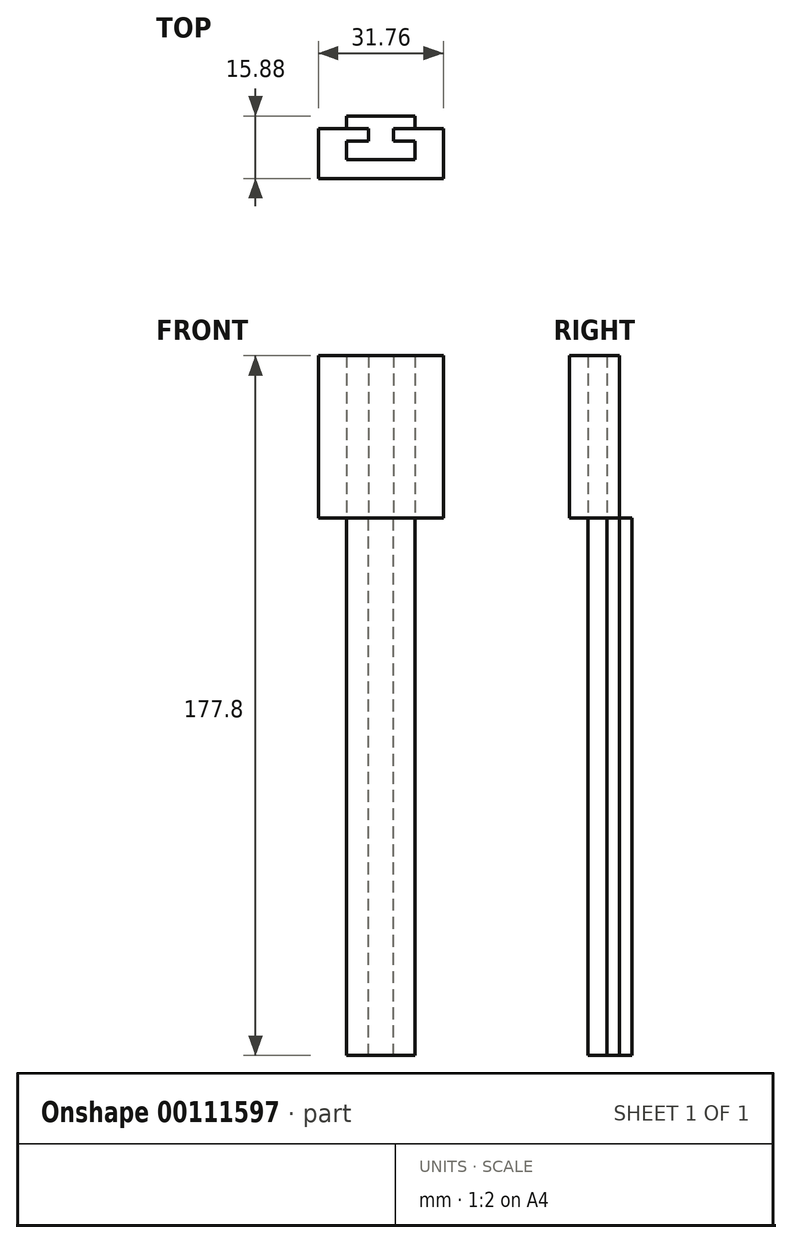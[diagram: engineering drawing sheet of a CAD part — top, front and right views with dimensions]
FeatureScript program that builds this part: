
annotation { "Feature Type Name" : "Feature", "Feature Type Description" : "" }
export const myFeature = defineFeature(function(context is Context, id is Id, definition is map)
    precondition{}
    {
        {
            var Q0;
            Q0=qCreatedBy(makeId("Top.planeOp"),FACE);
            var sketch = newSketch(context, id + "F0", { "sketchPlane" : qUnion([Q0])});
            skLineSegment(sketch, "E0.bottom", {"start": v(15.88, 6.35) * mm, "end": v(3.17, 6.35) * mm});
            skLineSegment(sketch, "E0.top", {"start": v(15.88, -6.35) * mm, "end": v(-15.88, -6.35) * mm});
            skLineSegment(sketch, "E0.left", {"start": v(15.88, 6.35) * mm, "end": v(15.88, -6.35) * mm});
            skLineSegment(sketch, "E0.right", {"start": v(-15.88, 6.35) * mm, "end": v(-15.88, -6.35) * mm});
            skPoint(sketch, "E0.middle", {"position": v(0, 0) * mm});
            skLineSegment(sketch, "E1", {"start": v(-3.17, 6.35) * mm, "end": v(-3.17, 3.17) * mm});
            skLineSegment(sketch, "E2", {"start": v(-3.17, 3.18) * mm, "end": v(-8.73, 3.18) * mm});
            skLineSegment(sketch, "E3", {"start": v(-8.73, 3.18) * mm, "end": v(-8.73, -1.59) * mm});
            skLineSegment(sketch, "E4", {"start": v(-8.73, -1.59) * mm, "end": v(8.73, -1.59) * mm});
            skLineSegment(sketch, "E5", {"start": v(8.73, -1.59) * mm, "end": v(8.73, 3.18) * mm});
            skLineSegment(sketch, "E6", {"start": v(8.73, 3.18) * mm, "end": v(3.17, 3.18) * mm});
            skLineSegment(sketch, "E7", {"start": v(3.17, 3.17) * mm, "end": v(3.17, 6.35) * mm});
            skPoint(sketch, "E8", {"position": v(0, -1.59) * mm});
            skLineSegment(sketch, "E9.trimOffspring", {"start": v(-3.17, 6.35) * mm, "end": v(-15.88, 6.35) * mm});
            skSolve(sketch);
        }
        {
            var Q0;
            Q0 = qSketchRegion(id + "F0", true);
            extrude(context, id + "F1", {"entities" : qUnion([Q0]), "depth" : 41.27 * mm});
        }
        {
            var Q0;
            Q0=makeQuery(id+"F1.opExtrude","CAP_FACE",FACE,{"disambiguationData":[OSD([sQuery(id+"F0.wireOp",EDGE,"E0.bottom"),sQuery(id+"F0.wireOp",EDGE,"E0.top"),sQuery(id+"F0.wireOp",EDGE,"E0.left"),sQuery(id+"F0.wireOp",EDGE,"E0.right"),sQuery(id+"F0.wireOp",EDGE,"E1"),sQuery(id+"F0.wireOp",EDGE,"E2"),sQuery(id+"F0.wireOp",EDGE,"E3"),sQuery(id+"F0.wireOp",EDGE,"E4"),sQuery(id+"F0.wireOp",EDGE,"E5"),sQuery(id+"F0.wireOp",EDGE,"E6"),sQuery(id+"F0.wireOp",EDGE,"E7"),sQuery(id+"F0.wireOp",EDGE,"E9.trimOffspring")])],"isStart":true});
            var sketch = newSketch(context, id + "F2", { "sketchPlane" : qUnion([Q0])});
            skLineSegment(sketch, "E10.0", {"start": v(8.73, -3.18) * mm, "end": v(3.17, -3.18) * mm});
            skLineSegment(sketch, "E10.1", {"start": v(8.73, 1.59) * mm, "end": v(8.73, -3.18) * mm});
            skLineSegment(sketch, "E10.2", {"start": v(-8.73, 1.59) * mm, "end": v(8.73, 1.59) * mm});
            skLineSegment(sketch, "E10.3", {"start": v(-8.73, -3.18) * mm, "end": v(-8.73, 1.59) * mm});
            skLineSegment(sketch, "E10.4", {"start": v(-3.17, -3.18) * mm, "end": v(-8.73, -3.18) * mm});
            skLineSegment(sketch, "E10.5", {"start": v(-3.17, -4.76) * mm, "end": v(-3.17, -3.18) * mm});
            skLineSegment(sketch, "E10.6", {"start": v(3.17, -3.17) * mm, "end": v(3.17, -4.76) * mm});
            skPoint(sketch, "E11", {"position": v(3.17, -4.76) * mm});
            skLineSegment(sketch, "E12", {"start": v(3.17, -4.76) * mm, "end": v(-3.17, -4.76) * mm, "construction": true});
            skPoint(sketch, "E13.orphan", {"position": v(3.17, -6.35) * mm});
            skPoint(sketch, "E14.orphan", {"position": v(-3.17, -6.35) * mm});
            skLineSegment(sketch, "E15.MirrorCS", {"start": v(3.18, -6.35) * mm, "end": v(3.17, -4.76) * mm});
            skLineSegment(sketch, "E16.MirrorCS", {"start": v(8.73, -9.53) * mm, "end": v(8.73, -6.35) * mm});
            skLineSegment(sketch, "E17.MirrorCS", {"start": v(8.73, -6.35) * mm, "end": v(3.17, -6.35) * mm});
            skLineSegment(sketch, "E18.MirrorCS", {"start": v(-8.73, -9.52) * mm, "end": v(8.73, -9.53) * mm});
            skLineSegment(sketch, "E19.MirrorCS", {"start": v(-8.73, -6.35) * mm, "end": v(-8.73, -9.53) * mm});
            skLineSegment(sketch, "E20.MirrorCS", {"start": v(-3.17, -4.76) * mm, "end": v(-3.17, -6.35) * mm});
            skLineSegment(sketch, "E21.MirrorCS", {"start": v(-3.17, -6.35) * mm, "end": v(-8.73, -6.35) * mm});
            skSolve(sketch);
        }
        {
            var Q0;
            Q0=makeQuery(id+"F2.imprint","IMPRINT",FACE,{"disambiguationData":[TD([[makeQuery(id+"F2.imprint","IMPRINT",EDGE,{"derivedFrom":sQuery(id+"F2.wireOp",EDGE,"E10.0")}),-1.0]])]});
            extrude(context, id + "F3", {"entities" : qUnion([Q0]), "depth" : 136.53 * mm});
        }
    });
